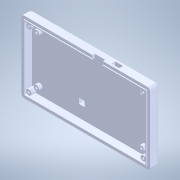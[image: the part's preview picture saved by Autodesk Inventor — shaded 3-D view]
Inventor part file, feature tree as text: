
AUTODESK INVENTOR PART (.ipt)
format: ipt  version: 2022 (Build 260153000, 153)  size: 166,912 bytes
history: native  units: mm
features: extrude x3, sketch x3, other x2
ambient origin geometry x8: Origin, YZ Plane, XZ Plane, XY Plane, X Axis, Y Axis, Z Axis, Center Point
bodies: Body1 (feature_tree)
feature tree (8):
  other  "Твердое тело1"
  extrude  "Выдавливание1"  Depth=5.0mm TaperAngle=0.0deg
  extrude  "Выдавливание2"  Depth=11.0mm
  extrude  "Выдавливание3"  Depth=10.0mm TaperAngle=0.0deg
  sketch  "Эскиз1"
  sketch  "Эскиз2"
  sketch  "Эскиз3"
  other  "Ñêðóãëåíèå1"
